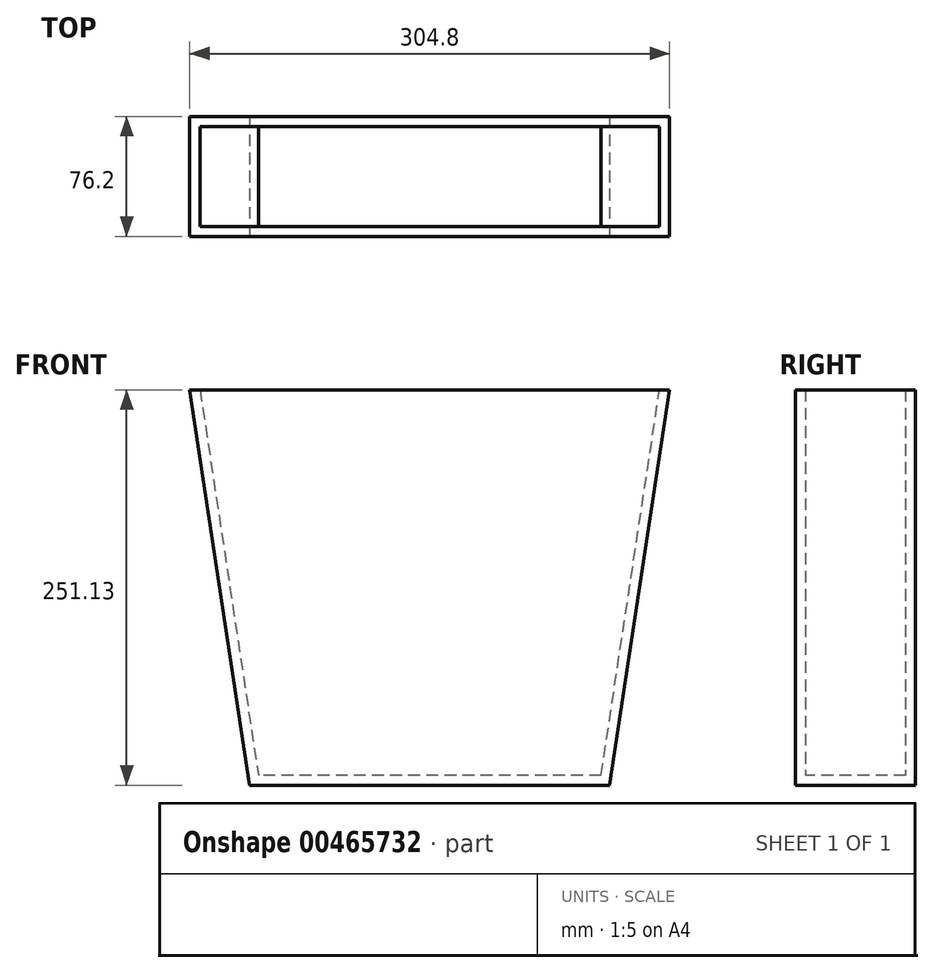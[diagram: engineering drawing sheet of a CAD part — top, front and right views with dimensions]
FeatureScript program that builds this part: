
annotation { "Feature Type Name" : "Feature", "Feature Type Description" : "" }
export const myFeature = defineFeature(function(context is Context, id is Id, definition is map)
    precondition{}
    {
        {
            var Q0;
            Q0=qCreatedBy(makeId("Front.planeOp"),FACE);
            var sketch = newSketch(context, id + "F0", { "sketchPlane" : qUnion([Q0])});
            skLineSegment(sketch, "E0", {"start": v(-232.28, 0) * mm, "end": v(-194.18, -251.13) * mm});
            skLineSegment(sketch, "E1", {"start": v(34.42, -251.13) * mm, "end": v(72.52, 0) * mm});
            skLineSegment(sketch, "E2", {"start": v(-79.88, 0) * mm, "end": v(-79.88, -251.13) * mm});
            skLineSegment(sketch, "E3", {"start": v(-232.28, 0) * mm, "end": v(-79.88, 0) * mm});
            skLineSegment(sketch, "E4", {"start": v(72.52, 0) * mm, "end": v(-79.88, 0) * mm});
            skLineSegment(sketch, "E5", {"start": v(-194.18, -251.13) * mm, "end": v(-79.88, -251.13) * mm});
            skLineSegment(sketch, "E6", {"start": v(34.42, -251.13) * mm, "end": v(-79.88, -251.13) * mm});
            skSolve(sketch);
        }
        {
            var Q0;
            Q0=makeQuery(id+"F0.imprint","IMPRINT",FACE,{"disambiguationData":[TD([[makeQuery(id+"F0.imprint","IMPRINT",EDGE,{"derivedFrom":sQuery(id+"F0.wireOp",EDGE,"E1")}),1.0]])]});
            var Q1;
            Q1=makeQuery(id+"F0.imprint","IMPRINT",FACE,{"disambiguationData":[TD([[makeQuery(id+"F0.imprint","IMPRINT",EDGE,{"derivedFrom":sQuery(id+"F0.wireOp",EDGE,"E0")}),1.0]])]});
            extrude(context, id + "F1", {"entities" : qUnion([Q0, Q1]), "oppositeDirection" : true, "depth" : 76.2 * mm});
        }
        {
            var Q0;
            Q0=makeQuery(id+"F1.opExtrude","SWEPT_FACE",FACE,{"disambiguationData":[OSD([sQuery(id+"F0.wireOp",EDGE,"E3"),sQuery(id+"F0.wireOp",EDGE,"E4")])]});
            shell(context, id + "F2", {"entities" : qUnion([Q0]), "thickness" : 6.35 * mm});
        }
    });
